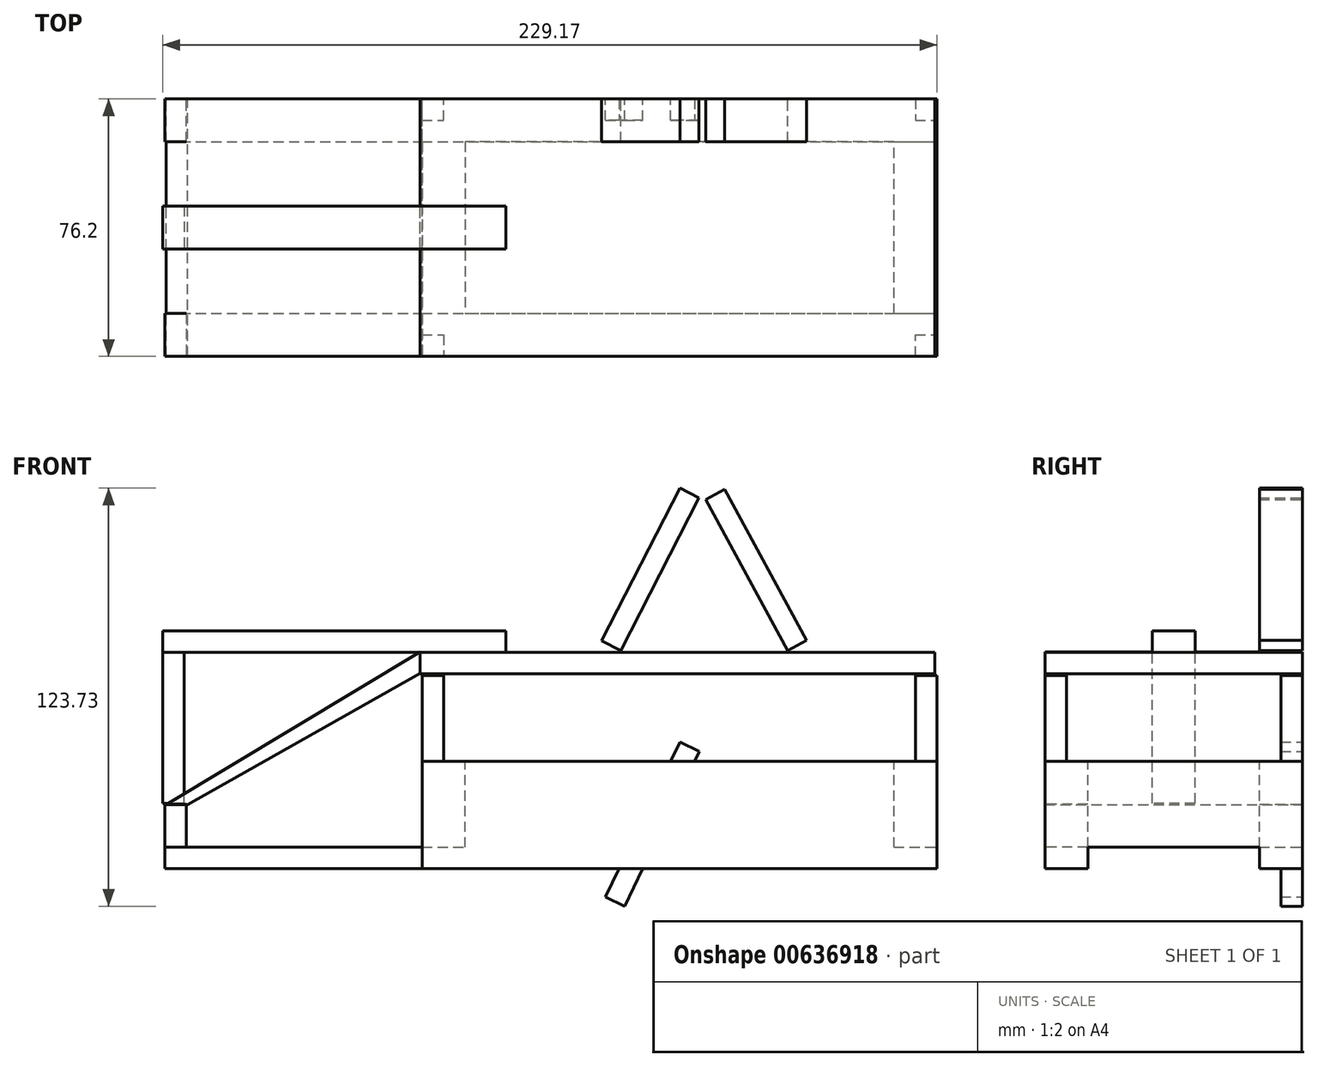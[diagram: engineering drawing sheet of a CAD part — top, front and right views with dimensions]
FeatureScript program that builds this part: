
annotation { "Feature Type Name" : "Feature", "Feature Type Description" : "" }
export const myFeature = defineFeature(function(context is Context, id is Id, definition is map)
    precondition{}
    {
        {
            var Q0;
            Q0=qCreatedBy(makeId("Front.planeOp"),FACE);
            var sketch = newSketch(context, id + "F0", { "sketchPlane" : qUnion([Q0])});
            skLineSegment(sketch, "E0", {"start": v(-76.33, 0) * mm, "end": v(76.07, 0) * mm});
            skLineSegment(sketch, "E1", {"start": v(76.07, 0) * mm, "end": v(76.07, -31.75) * mm});
            skLineSegment(sketch, "E2", {"start": v(76.07, -31.75) * mm, "end": v(-76.33, -31.75) * mm});
            skLineSegment(sketch, "E3", {"start": v(-76.33, -31.75) * mm, "end": v(-76.33, 0) * mm});
            skLineSegment(sketch, "E4", {"start": v(-76.33, -25.4) * mm, "end": v(76.07, -25.4) * mm});
            skSolve(sketch);
        }
        {
            var Q0;
            Q0 = qSketchRegion(id + "F0", true);
            extrude(context, id + "F1", {"entities" : qUnion([Q0]), "depth" : 76.2 * mm, "offsetDistance" : 25.4 * mm});
        }
        {
            var Q0;
            Q0=makeQuery(id+"F1.opExtrude","SWEPT_FACE",FACE,{"disambiguationData":[OSD([sQuery(id+"F0.wireOp",EDGE,"E1")])]});
            var sketch = newSketch(context, id + "F2", { "sketchPlane" : qUnion([Q0])});
            skLineSegment(sketch, "E5", {"start": v(-63.5, -31.75) * mm, "end": v(-63.5, -25.4) * mm});
            skLineSegment(sketch, "E6", {"start": v(-63.5, -25.4) * mm, "end": v(-12.7, -25.4) * mm});
            skLineSegment(sketch, "E7", {"start": v(-12.7, -25.4) * mm, "end": v(-12.7, -31.75) * mm});
            skLineSegment(sketch, "E8", {"start": v(-63.5, -31.75) * mm, "end": v(-12.7, -31.75) * mm});
            skSolve(sketch);
        }
        {
            var Q0;
            Q0 = qSketchRegion(id + "F2", true);
            extrude(context, id + "F3", {"entities" : qUnion([Q0]), "operationType" : NewBodyOperationType.REMOVE, "oppositeDirection" : true, "depth" : 175 * mm, "offsetDistance" : 25.4 * mm});
        }
        {
            var Q0;
            Q0=makeQuery(id+"F1.opExtrude","SWEPT_FACE",FACE,{"disambiguationData":[OSD([sQuery(id+"F0.wireOp",EDGE,"E0")])]});
            var sketch = newSketch(context, id + "F4", { "sketchPlane" : qUnion([Q0])});
            skLineSegment(sketch, "E9", {"start": v(-63.63, -12.7) * mm, "end": v(-63.63, -63.5) * mm});
            skLineSegment(sketch, "E10", {"start": v(-63.63, -63.5) * mm, "end": v(63.37, -63.5) * mm});
            skLineSegment(sketch, "E11", {"start": v(63.37, -63.5) * mm, "end": v(63.37, -12.7) * mm});
            skLineSegment(sketch, "E12", {"start": v(63.37, -12.7) * mm, "end": v(-63.63, -12.7) * mm});
            skSolve(sketch);
        }
        {
            var Q0;
            Q0 = qSketchRegion(id + "F4", true);
            extrude(context, id + "F5", {"entities" : qUnion([Q0]), "operationType" : NewBodyOperationType.REMOVE, "oppositeDirection" : true, "depth" : 43.69 * mm, "offsetDistance" : 25.4 * mm});
        }
        {
            var Q0;
            Q0=makeQuery(id+"F1.opExtrude","SWEPT_FACE",FACE,{"disambiguationData":[OSD([sQuery(id+"F0.wireOp",EDGE,"E0")])]});
            var sketch = newSketch(context, id + "F6", { "sketchPlane" : qUnion([Q0])});
            skLineSegment(sketch, "E13", {"start": v(-76.33, -6.35) * mm, "end": v(-69.98, -6.35) * mm});
            skLineSegment(sketch, "E14", {"start": v(-69.98, -6.35) * mm, "end": v(-69.98, 0) * mm});
            skLineSegment(sketch, "E15", {"start": v(-76.33, -69.85) * mm, "end": v(-69.98, -69.85) * mm});
            skLineSegment(sketch, "E16", {"start": v(-69.98, -69.85) * mm, "end": v(-69.98, -76.2) * mm});
            skLineSegment(sketch, "E17", {"start": v(69.72, 0) * mm, "end": v(69.72, -6.35) * mm});
            skLineSegment(sketch, "E18", {"start": v(69.72, -6.35) * mm, "end": v(76.07, -6.35) * mm});
            skLineSegment(sketch, "E19", {"start": v(69.72, -76.2) * mm, "end": v(69.72, -69.85) * mm});
            skLineSegment(sketch, "E20", {"start": v(69.72, -69.85) * mm, "end": v(76.07, -69.85) * mm});
            skSolve(sketch);
        }
        {
            var Q0;
            Q0 = qSketchRegion(id + "F6", true);
            var Q1;
            {var subQ0=sQuery(id+"F6.wireOp",EDGE,"E13");Q1=makeQuery(id+"F6.imprint","IMPRINT",FACE,{"disambiguationData":[TD([[makeQuery(id+"F6.imprint","IMPRINT",EDGE,{"derivedFrom":subQ0}),1.0]])]});}
            extrude(context, id + "F7", {"entities" : qUnion([Q0, Q1]), "depth" : 25.4 * mm, "offsetDistance" : 25.4 * mm});
        }
        {
            var Q0;
            {var subQ0=sQuery(id+"F6.wireOp",EDGE,"E15");Q0=makeQuery(id+"F6.imprint","IMPRINT",FACE,{"disambiguationData":[TD([[makeQuery(id+"F6.imprint","IMPRINT",EDGE,{"derivedFrom":subQ0}),-1.0]])]});}
            extrude(context, id + "F8", {"entities" : qUnion([Q0]), "depth" : 25.4 * mm, "offsetDistance" : 25.4 * mm});
        }
        {
            var Q0;
            {var subQ0=sQuery(id+"F6.wireOp",EDGE,"E17");Q0=makeQuery(id+"F6.imprint","IMPRINT",FACE,{"disambiguationData":[TD([[makeQuery(id+"F6.imprint","IMPRINT",EDGE,{"derivedFrom":subQ0}),1.0]])]});}
            extrude(context, id + "F9", {"entities" : qUnion([Q0]), "depth" : 25.4 * mm, "offsetDistance" : 25.4 * mm});
        }
        {
            var Q0;
            {var subQ0=sQuery(id+"F6.wireOp",EDGE,"E19");Q0=makeQuery(id+"F6.imprint","IMPRINT",FACE,{"disambiguationData":[TD([[makeQuery(id+"F6.imprint","IMPRINT",EDGE,{"derivedFrom":subQ0}),-1.0]])]});}
            extrude(context, id + "F10", {"entities" : qUnion([Q0]), "depth" : 25.4 * mm, "offsetDistance" : 25.4 * mm});
        }
        {
            var Q0;
            Q0=qCreatedBy(makeId("Front.planeOp"),FACE);
            var sketch = newSketch(context, id + "F11", { "sketchPlane" : qUnion([Q0])});
            skLineSegment(sketch, "E21", {"start": v(-76.9, 26.02) * mm, "end": v(75.5, 26.02) * mm});
            skLineSegment(sketch, "E22", {"start": v(75.5, 26.02) * mm, "end": v(75.5, 32.37) * mm});
            skLineSegment(sketch, "E23", {"start": v(75.5, 32.37) * mm, "end": v(-76.9, 32.37) * mm});
            skLineSegment(sketch, "E24", {"start": v(-76.9, 32.37) * mm, "end": v(-76.9, 26.02) * mm});
            skSolve(sketch);
        }
        {
            var Q0;
            Q0 = qSketchRegion(id + "F11", true);
            extrude(context, id + "F12", {"entities" : qUnion([Q0]), "depth" : 76.2 * mm, "offsetDistance" : 25.4 * mm});
        }
        {
            var Q0;
            Q0=makeQuery(id+"F12.opExtrude","SWEPT_FACE",FACE,{"disambiguationData":[OSD([sQuery(id+"F11.wireOp",EDGE,"E23")])]});
            var sketch = newSketch(context, id + "F13", { "sketchPlane" : qUnion([Q0])});
            skLineSegment(sketch, "E25", {"start": v(-153.1, -31.75) * mm, "end": v(-51.5, -31.75) * mm});
            skLineSegment(sketch, "E26", {"start": v(-51.5, -31.75) * mm, "end": v(-51.5, -44.45) * mm});
            skLineSegment(sketch, "E27", {"start": v(-51.5, -44.45) * mm, "end": v(-153.1, -44.45) * mm});
            skLineSegment(sketch, "E28", {"start": v(-153.1, -44.45) * mm, "end": v(-153.1, -31.75) * mm});
            skSolve(sketch);
        }
        {
            var Q0;
            Q0 = qSketchRegion(id + "F13", true);
            extrude(context, id + "F14", {"entities" : qUnion([Q0]), "operationType" : NewBodyOperationType.ADD, "depth" : 6.35 * mm, "offsetDistance" : 25.4 * mm});
        }
        {
            var Q0;
            Q0=makeQuery(id+"F1.opExtrude","SWEPT_FACE",FACE,{"disambiguationData":[OSD([sQuery(id+"F0.wireOp",EDGE,"E3")])]});
            var sketch = newSketch(context, id + "F15", { "sketchPlane" : qUnion([Q0])});
            skLineSegment(sketch, "E29", {"start": v(12.7, -25.4) * mm, "end": v(0, -25.4) * mm});
            skSolve(sketch);
        }
        {
            var Q0;
            Q0 = qSketchRegion(id + "F15", true);
            var Q1;
            {var subQ0=sQuery(id+"F15.wireOp",EDGE,"E29");Q1=makeQuery(id+"F15.imprint","IMPRINT",FACE,{"disambiguationData":[TD([[makeQuery(id+"F15.imprint","IMPRINT",EDGE,{"derivedFrom":subQ0}),1.0]])]});}
            extrude(context, id + "F16", {"entities" : qUnion([Q0, Q1]), "depth" : 76.2 * mm, "offsetDistance" : 25.4 * mm});
        }
        {
            var Q0;
            Q0=makeQuery(id+"F1.opExtrude","SWEPT_FACE",FACE,{"disambiguationData":[OSD([sQuery(id+"F0.wireOp",EDGE,"E3")])]});
            var sketch = newSketch(context, id + "F17", { "sketchPlane" : qUnion([Q0])});
            skLineSegment(sketch, "E30", {"start": v(63.5, -25.4) * mm, "end": v(76.2, -25.4) * mm});
            skSolve(sketch);
        }
        {
            var Q0;
            {var subQ4=sQuery(id+"F17.wireOp",EDGE,"E30");Q0=makeQuery(id+"F17.imprint","IMPRINT",FACE,{"disambiguationData":[TD([[makeQuery(id+"F17.imprint","IMPRINT",EDGE,{"derivedFrom":subQ4}),1.0]])]});}
            var sketch = newSketch(context, id + "F18", { "sketchPlane" : qUnion([Q0])});
            skLineSegment(sketch, "E31", {"start": v(63.37, -25.02) * mm, "end": v(76.07, -25.02) * mm});
            skSolve(sketch);
        }
        {
            var Q0;
            Q0 = qSketchRegion(id + "F18", true);
            var Q1;
            {var subQ0=sQuery(id+"F17.wireOp",EDGE,"E30");Q1=makeQuery(id+"F17.imprint","IMPRINT",FACE,{"disambiguationData":[TD([[makeQuery(id+"F17.imprint","IMPRINT",EDGE,{"derivedFrom":subQ0}),-1.0]])]});}
            extrude(context, id + "F19", {"entities" : qUnion([Q0, Q1]), "depth" : 76.2 * mm, "offsetDistance" : 25.4 * mm});
        }
        {
            var Q0;
            Q0=makeQuery(id+"F16.opExtrude","SWEPT_FACE",FACE,{"disambiguationData":[OSD([sQuery(id+"F0.wireOp",EDGE,"E3")])]});
            var sketch = newSketch(context, id + "F20", { "sketchPlane" : qUnion([Q0])});
            skLineSegment(sketch, "E32", {"start": v(146.18, -25.4) * mm, "end": v(146.18, -12.7) * mm});
            skLineSegment(sketch, "E33", {"start": v(146.18, -12.7) * mm, "end": v(152.53, -12.7) * mm});
            skLineSegment(sketch, "E34", {"start": v(152.53, -12.7) * mm, "end": v(152.53, -25.4) * mm});
            skLineSegment(sketch, "E35", {"start": v(152.53, -25.4) * mm, "end": v(146.18, -25.4) * mm});
            skSolve(sketch);
        }
        {
            var Q0;
            Q0 = qSketchRegion(id + "F20", true);
            extrude(context, id + "F21", {"entities" : qUnion([Q0]), "oppositeDirection" : true, "depth" : 12.7 * mm, "offsetDistance" : 25.4 * mm});
        }
        {
            var Q0;
            Q0=makeQuery(id+"F19.opExtrude","CAP_FACE",FACE,{"disambiguationData":[OSD([sQuery(id+"F0.wireOp",EDGE,"E2"),sQuery(id+"F0.wireOp",EDGE,"E3"),sQuery(id+"F2.wireOp",EDGE,"E5"),sQuery(id+"F17.wireOp",EDGE,"E30")])],"isStart":false});
            var sketch = newSketch(context, id + "F22", { "sketchPlane" : qUnion([Q0])});
            skLineSegment(sketch, "E36", {"start": v(63.5, -25.4) * mm, "end": v(63.5, -12.7) * mm});
            skLineSegment(sketch, "E37", {"start": v(63.5, -12.7) * mm, "end": v(76.2, -12.7) * mm});
            skLineSegment(sketch, "E38", {"start": v(76.2, -12.7) * mm, "end": v(76.2, -25.4) * mm});
            skLineSegment(sketch, "E39", {"start": v(76.2, -25.4) * mm, "end": v(63.5, -25.4) * mm});
            skSolve(sketch);
        }
        {
            var Q0;
            Q0 = qSketchRegion(id + "F22", true);
            extrude(context, id + "F23", {"entities" : qUnion([Q0]), "oppositeDirection" : true, "depth" : 6.35 * mm, "offsetDistance" : 25.4 * mm});
        }
        {
            var Q0;
            Q0=qCreatedBy(makeId("Front.planeOp"),FACE);
            var sketch = newSketch(context, id + "F24", { "sketchPlane" : qUnion([Q0])});
            skLineSegment(sketch, "E40", {"start": v(-145.77, -12.83) * mm, "end": v(-76.93, 26.03) * mm});
            skLineSegment(sketch, "E41", {"start": v(-76.93, 26.03) * mm, "end": v(-76.93, 32.38) * mm});
            skLineSegment(sketch, "E42", {"start": v(-76.93, 32.38) * mm, "end": v(-152.12, -12.83) * mm});
            skLineSegment(sketch, "E43", {"start": v(-152.12, -12.83) * mm, "end": v(-145.77, -12.83) * mm});
            skSolve(sketch);
        }
        {
            var Q0;
            Q0 = qSketchRegion(id + "F24", true);
            extrude(context, id + "F25", {"entities" : qUnion([Q0]), "depth" : 76.2 * mm, "offsetDistance" : 25.4 * mm});
        }
        {
            var Q0;
            Q0=makeQuery(id+"F14.opExtrude","CAP_FACE",FACE,{"disambiguationData":[OSD([sQuery(id+"F13.wireOp",EDGE,"E25"),sQuery(id+"F13.wireOp",EDGE,"E26"),sQuery(id+"F13.wireOp",EDGE,"E27"),sQuery(id+"F13.wireOp",EDGE,"E28")])],"isStart":true});
            var sketch = newSketch(context, id + "F26", { "sketchPlane" : qUnion([Q0])});
            skLineSegment(sketch, "E44", {"start": v(-146.75, 31.75) * mm, "end": v(-146.75, 44.45) * mm});
            skLineSegment(sketch, "E45", {"start": v(-146.75, 44.45) * mm, "end": v(-153.1, 44.45) * mm});
            skLineSegment(sketch, "E46", {"start": v(-153.1, 44.45) * mm, "end": v(-153.1, 31.75) * mm});
            skLineSegment(sketch, "E47", {"start": v(-153.1, 31.75) * mm, "end": v(-146.75, 31.75) * mm});
            skSolve(sketch);
        }
        {
            var Q0;
            Q0 = qSketchRegion(id + "F26", true);
            extrude(context, id + "F27", {"entities" : qUnion([Q0]), "depth" : 44.7 * mm, "offsetDistance" : 25.4 * mm});
        }
        {
            var Q0;
            Q0=qCreatedBy(makeId("Front.planeOp"),FACE);
            var sketch = newSketch(context, id + "F28", { "sketchPlane" : qUnion([Q0])});
            skLineSegment(sketch, "E48", {"start": v(-23.17, 35.69) * mm, "end": v(0, 80.9) * mm});
            skLineSegment(sketch, "E49", {"start": v(0, 80.9) * mm, "end": v(5.65, 78) * mm});
            skLineSegment(sketch, "E50", {"start": v(5.65, 78) * mm, "end": v(-17.52, 32.8) * mm});
            skLineSegment(sketch, "E51", {"start": v(-17.52, 32.8) * mm, "end": v(-23.17, 35.69) * mm});
            skSolve(sketch);
        }
        {
            var Q0;
            Q0 = qSketchRegion(id + "F28", true);
            extrude(context, id + "F29", {"entities" : qUnion([Q0]), "depth" : 12.7 * mm, "offsetDistance" : 25.4 * mm});
        }
        {
            var Q0;
            Q0=qCreatedBy(makeId("Front.planeOp"),FACE);
            var sketch = newSketch(context, id + "F30", { "sketchPlane" : qUnion([Q0])});
            skLineSegment(sketch, "E52", {"start": v(13.26, 80.52) * mm, "end": v(7.68, 77.5) * mm});
            skLineSegment(sketch, "E53", {"start": v(7.68, 77.5) * mm, "end": v(31.88, 32.83) * mm});
            skLineSegment(sketch, "E54", {"start": v(31.88, 32.83) * mm, "end": v(37.46, 35.86) * mm});
            skLineSegment(sketch, "E55", {"start": v(37.46, 35.86) * mm, "end": v(13.26, 80.52) * mm});
            skSolve(sketch);
        }
        {
            var Q0;
            Q0 = qSketchRegion(id + "F30", true);
            extrude(context, id + "F31", {"entities" : qUnion([Q0]), "depth" : 12.7 * mm, "offsetDistance" : 25.4 * mm});
        }
        {
            var Q0;
            Q0=qCreatedBy(makeId("Front.planeOp"),FACE);
            var sketch = newSketch(context, id + "F32", { "sketchPlane" : qUnion([Q0])});
            skLineSegment(sketch, "E56", {"start": v(-22.03, -40.08) * mm, "end": v(-16.3, -42.83) * mm});
            skLineSegment(sketch, "E57", {"start": v(-16.3, -42.83) * mm, "end": v(5.72, 2.95) * mm});
            skLineSegment(sketch, "E58", {"start": v(5.72, 2.95) * mm, "end": v(0, 5.7) * mm});
            skLineSegment(sketch, "E59", {"start": v(0, 5.7) * mm, "end": v(-22.03, -40.08) * mm});
            skSolve(sketch);
        }
        {
            var Q0;
            Q0 = qSketchRegion(id + "F32", true);
            extrude(context, id + "F33", {"entities" : qUnion([Q0]), "operationType" : NewBodyOperationType.ADD, "depth" : 6.35 * mm, "offsetDistance" : 25.4 * mm});
        }
    });
